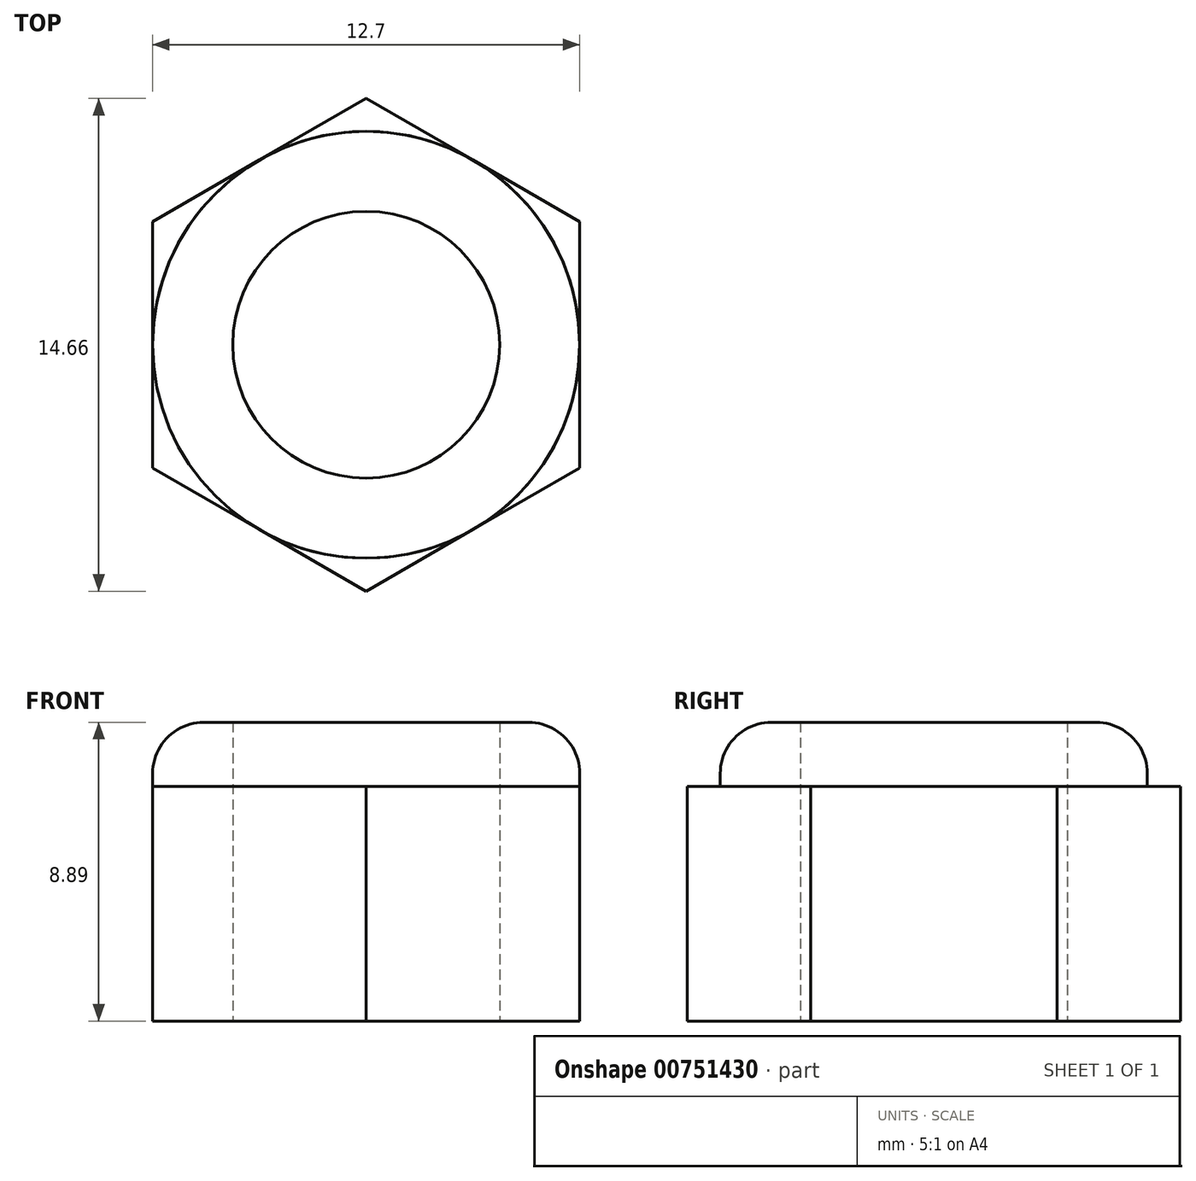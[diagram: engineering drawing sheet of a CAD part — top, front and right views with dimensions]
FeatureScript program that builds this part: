
annotation { "Feature Type Name" : "Feature", "Feature Type Description" : "" }
export const myFeature = defineFeature(function(context is Context, id is Id, definition is map)
    precondition{}
    {
        {
            var Q0;
            Q0=qCreatedBy(makeId("Top.planeOp"),FACE);
            var sketch = newSketch(context, id + "F0", { "sketchPlane" : qUnion([Q0])});
            skCircle(sketch, "E0.cCircle", {"center": v(0, 0) * mm, "radius": 6.35 * mm});
            skLineSegment(sketch, "E0.0", {"start": v(6.35, 3.67) * mm, "end": v(6.35, -3.67) * mm});
            skLineSegment(sketch, "E0.1", {"start": v(6.35, -3.67) * mm, "end": v(0, -7.33) * mm});
            skLineSegment(sketch, "E0.2", {"start": v(0, -7.33) * mm, "end": v(-6.35, -3.67) * mm});
            skLineSegment(sketch, "E0.3", {"start": v(-6.35, -3.67) * mm, "end": v(-6.35, 3.67) * mm});
            skLineSegment(sketch, "E0.4", {"start": v(-6.35, 3.67) * mm, "end": v(0, 7.33) * mm});
            skLineSegment(sketch, "E0.5", {"start": v(0, 7.33) * mm, "end": v(6.35, 3.67) * mm});
            skPoint(sketch, "E0.0.midPoint", {"position": v(6.35, 0) * mm});
            skCircle(sketch, "E1", {"center": v(0, 0) * mm, "radius": 3.97 * mm});
            skSolve(sketch);
        }
        {
            var Q0;
            {var subQ0=sQuery(id+"F0.wireOp",EDGE,"E0.3");var subQ1=sQuery(id+"F0.wireOp",EDGE,"E0.cCircle");var subQ2=makeQuery(id+"F0.imprint","INTERSECT",VERTEX,{"derivedFrom":[subQ1,subQ0]});Q0=makeQuery(id+"F0.imprint","IMPRINT",FACE,{"disambiguationData":[TD([[makeQuery(id+"F0.imprint","IMPRINT",EDGE,{"disambiguationData":[TD([[subQ2,-1.0]])],"derivedFrom":subQ1}),-1.0]])]});}
            var Q1;
            {var subQ0=sQuery(id+"F0.wireOp",EDGE,"E0.4");var subQ1=sQuery(id+"F0.wireOp",EDGE,"E0.cCircle");var subQ2=makeQuery(id+"F0.imprint","INTERSECT",VERTEX,{"derivedFrom":[subQ1,subQ0]});Q1=makeQuery(id+"F0.imprint","IMPRINT",FACE,{"disambiguationData":[TD([[makeQuery(id+"F0.imprint","IMPRINT",EDGE,{"disambiguationData":[TD([[subQ2,-1.0]])],"derivedFrom":subQ1}),-1.0]])]});}
            var Q2;
            {var subQ0=sQuery(id+"F0.wireOp",EDGE,"E0.5");var subQ1=sQuery(id+"F0.wireOp",EDGE,"E0.cCircle");var subQ2=makeQuery(id+"F0.imprint","INTERSECT",VERTEX,{"derivedFrom":[subQ1,subQ0]});Q2=makeQuery(id+"F0.imprint","IMPRINT",FACE,{"disambiguationData":[TD([[makeQuery(id+"F0.imprint","IMPRINT",EDGE,{"disambiguationData":[TD([[subQ2,-1.0]])],"derivedFrom":subQ1}),-1.0]])]});}
            var Q3;
            {var subQ0=sQuery(id+"F0.wireOp",EDGE,"E0.5");var subQ1=sQuery(id+"F0.wireOp",EDGE,"E0.cCircle");var subQ2=makeQuery(id+"F0.imprint","INTERSECT",VERTEX,{"derivedFrom":[subQ1,subQ0]});Q3=makeQuery(id+"F0.imprint","IMPRINT",FACE,{"disambiguationData":[TD([[makeQuery(id+"F0.imprint","IMPRINT",EDGE,{"disambiguationData":[TD([[subQ2,1.0]])],"derivedFrom":subQ1}),-1.0]])]});}
            var Q4;
            {var subQ0=sQuery(id+"F0.wireOp",EDGE,"E0.0");var subQ1=sQuery(id+"F0.wireOp",EDGE,"E0.cCircle");var subQ2=makeQuery(id+"F0.imprint","INTERSECT",VERTEX,{"derivedFrom":[subQ1,subQ0]});Q4=makeQuery(id+"F0.imprint","IMPRINT",FACE,{"disambiguationData":[TD([[makeQuery(id+"F0.imprint","IMPRINT",EDGE,{"disambiguationData":[TD([[subQ2,1.0]])],"derivedFrom":subQ1}),-1.0]])]});}
            var Q5;
            {var subQ0=sQuery(id+"F0.wireOp",EDGE,"E0.2");var subQ1=sQuery(id+"F0.wireOp",EDGE,"E0.cCircle");var subQ2=makeQuery(id+"F0.imprint","INTERSECT",VERTEX,{"derivedFrom":[subQ1,subQ0]});Q5=makeQuery(id+"F0.imprint","IMPRINT",FACE,{"disambiguationData":[TD([[makeQuery(id+"F0.imprint","IMPRINT",EDGE,{"disambiguationData":[TD([[subQ2,-1.0]])],"derivedFrom":subQ1}),-1.0]])]});}
            var Q6;
            Q6=makeQuery(id+"F0.imprint","IMPRINT",FACE,{"disambiguationData":[TD([[makeQuery(id+"F0.imprint","IMPRINT",EDGE,{"derivedFrom":sQuery(id+"F0.wireOp",EDGE,"E1")}),-1.0]])]});
            extrude(context, id + "F1", {"entities" : qUnion([Q0, Q1, Q2, Q3, Q4, Q5, Q6]), "depth" : 7 * mm, "offsetDistance" : 25.4 * mm});
        }
        {
            var Q0;
            Q0=makeQuery(id+"F0.imprint","IMPRINT",FACE,{"disambiguationData":[TD([[makeQuery(id+"F0.imprint","IMPRINT",EDGE,{"derivedFrom":sQuery(id+"F0.wireOp",EDGE,"E1")}),-1.0]])]});
            extrude(context, id + "F2", {"entities" : qUnion([Q0]), "operationType" : NewBodyOperationType.ADD, "depth" : 8.9 * mm, "offsetDistance" : 25.4 * mm});
        }
        {
            var Q0;
            Q0=makeQuery(id+"F2.opExtrude","CAP_EDGE",EDGE,{"disambiguationData":[OSD([sQuery(id+"F0.wireOp",EDGE,"E0.cCircle")])],"isStart":false});
            fillet(context, id + "F3", {"entities" : qUnion([Q0]), "radius" : 1.52 * mm, "tangentPropagation" : true, "allowEdgeOverflow" : false});
        }
    });
